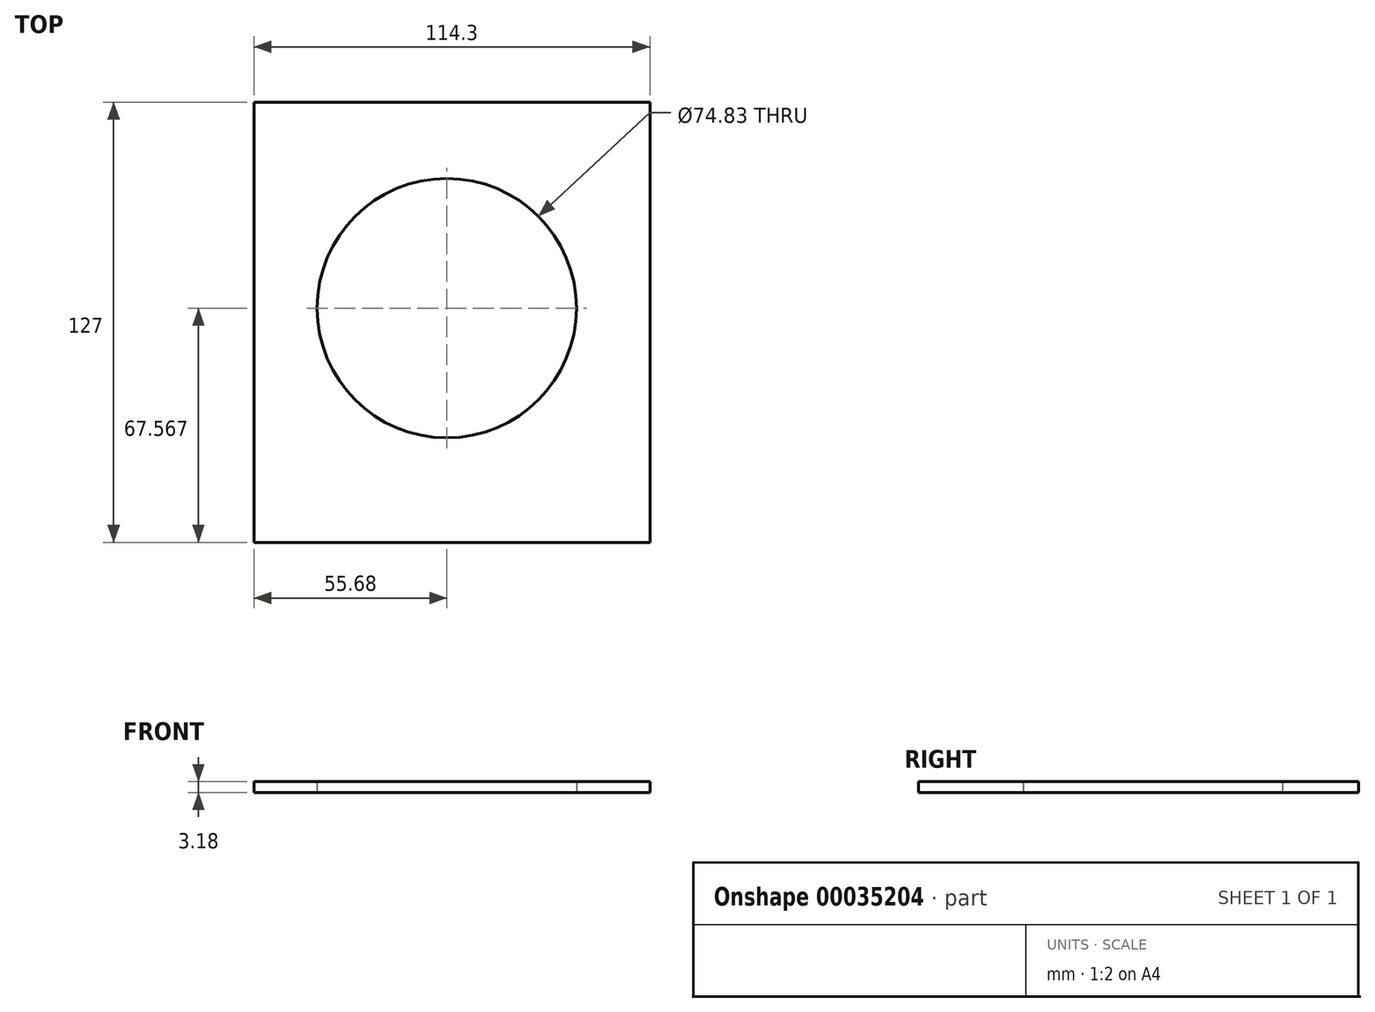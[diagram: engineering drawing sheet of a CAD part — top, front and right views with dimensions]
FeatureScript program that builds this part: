
annotation { "Feature Type Name" : "Feature", "Feature Type Description" : "" }
export const myFeature = defineFeature(function(context is Context, id is Id, definition is map)
    precondition{}
    {
        {
            var Q0;
            Q0=qCreatedBy(makeId("Top.planeOp"),FACE);
            var sketch = newSketch(context, id + "F0", { "sketchPlane" : qUnion([Q0])});
            skLineSegment(sketch, "E0.bottom", {"start": v(-55.68, 67.49) * mm, "end": v(58.62, 67.49) * mm});
            skLineSegment(sketch, "E0.top", {"start": v(-55.68, -59.51) * mm, "end": v(58.62, -59.51) * mm});
            skLineSegment(sketch, "E0.left", {"start": v(-55.68, 67.49) * mm, "end": v(-55.68, -59.51) * mm});
            skLineSegment(sketch, "E0.right", {"start": v(58.62, 67.49) * mm, "end": v(58.62, -59.51) * mm});
            skCircle(sketch, "E1", {"center": v(0, 8.06) * mm, "radius": 37.41 * mm});
            skSolve(sketch);
        }
        {
            var Q0;
            Q0=makeQuery(id+"F0.imprint","IMPRINT",FACE,{"disambiguationData":[TD([[makeQuery(id+"F0.imprint","IMPRINT",EDGE,{"derivedFrom":sQuery(id+"F0.wireOp",EDGE,"E0.bottom")}),-1.0]])]});
            extrude(context, id + "F1", {"entities" : qUnion([Q0]), "depth" : 3.18 * mm});
        }
    });
